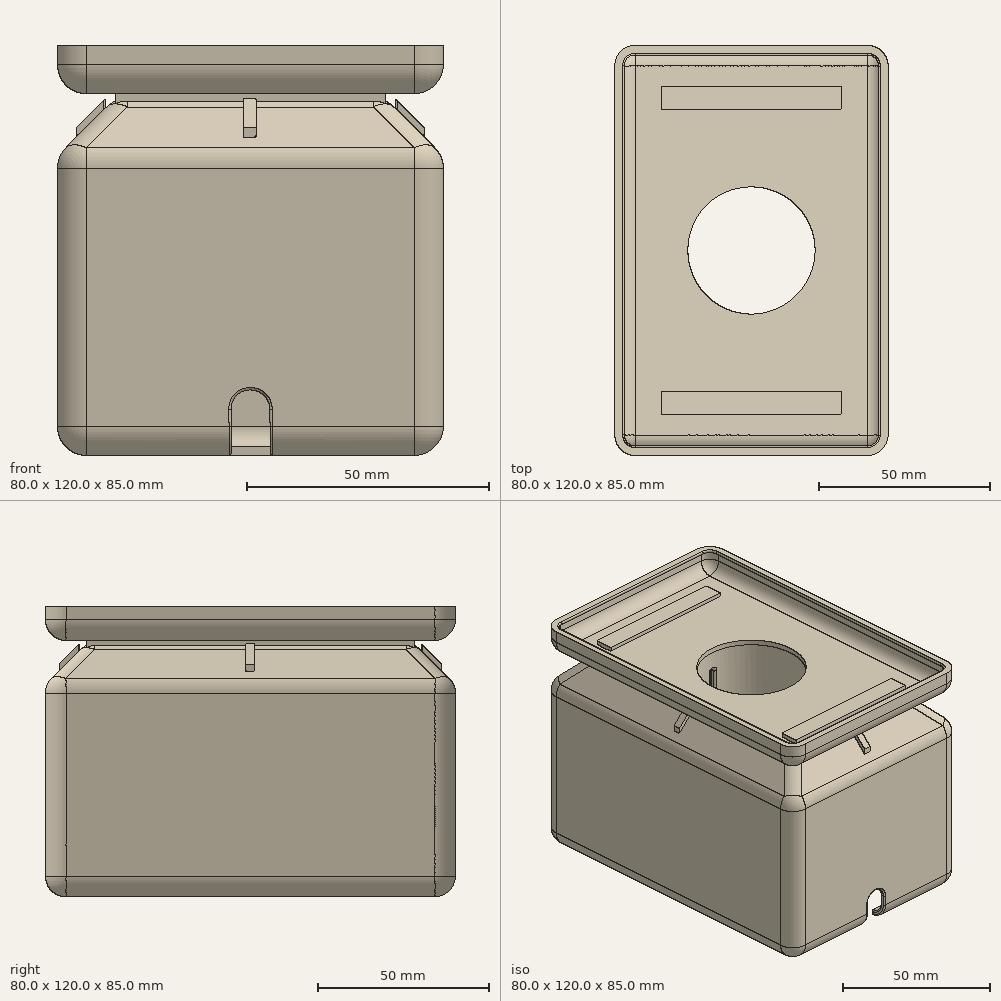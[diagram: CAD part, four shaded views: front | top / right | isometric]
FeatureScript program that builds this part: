
annotation { "Feature Type Name" : "Feature", "Feature Type Description" : "" }
export const myFeature = defineFeature(function(context is Context, id is Id, definition is map)
    precondition{}
    {
        {
            var Q0;
            Q0=qCreatedBy(makeId("Top.planeOp"),FACE);
            var sketch = newSketch(context, id + "F0", { "sketchPlane" : qUnion([Q0])});
            skLineSegment(sketch, "E0.bottom", {"start": v(0, 0) * mm, "end": v(80, 0) * mm});
            skLineSegment(sketch, "E0.top", {"start": v(0, 120) * mm, "end": v(80, 120) * mm});
            skLineSegment(sketch, "E0.left", {"start": v(0, 0) * mm, "end": v(0, 120) * mm});
            skLineSegment(sketch, "E0.right", {"start": v(80, 0) * mm, "end": v(80, 120) * mm});
            skSolve(sketch);
        }
        {
            var Q0;
            Q0=makeQuery(id+"F0.imprint","IMPRINT",FACE,{"disambiguationData":[TD([[makeQuery(id+"F0.imprint","IMPRINT",EDGE,{"derivedFrom":sQuery(id+"F0.wireOp",EDGE,"E0.bottom")}),1.0]])]});
            extrude(context, id + "F1", {"entities" : qUnion([Q0]), "oppositeDirection" : true, "depth" : 12 * mm});
        }
        {
            var Q0;
            Q0=makeQuery(id+"F1.opExtrude","CAP_FACE",FACE,{"disambiguationData":[OSD([sQuery(id+"F0.wireOp",EDGE,"E0.bottom"),sQuery(id+"F0.wireOp",EDGE,"E0.top"),sQuery(id+"F0.wireOp",EDGE,"E0.left"),sQuery(id+"F0.wireOp",EDGE,"E0.right")])],"isStart":true});
            chamfer(context, id + "F2", {"entities" : qUnion([Q0]), "width" : 12 * mm, "tangentPropagation" : true});
        }
        {
            var Q0;
            Q0=makeQuery(id+"F1.opExtrude","CAP_FACE",FACE,{"disambiguationData":[OSD([sQuery(id+"F0.wireOp",EDGE,"E0.bottom"),sQuery(id+"F0.wireOp",EDGE,"E0.top"),sQuery(id+"F0.wireOp",EDGE,"E0.left"),sQuery(id+"F0.wireOp",EDGE,"E0.right")])],"isStart":false});
            extrude(context, id + "F3", {"entities" : qUnion([Q0]), "operationType" : NewBodyOperationType.ADD, "depth" : 62 * mm});
        }
        {
            var Q0;
            Q0=makeQuery(id+"F3.opExtrude","CAP_FACE",FACE,{"disambiguationData":[OSD([sQuery(id+"F0.wireOp",EDGE,"E0.bottom"),sQuery(id+"F0.wireOp",EDGE,"E0.top"),sQuery(id+"F0.wireOp",EDGE,"E0.left"),sQuery(id+"F0.wireOp",EDGE,"E0.right")])],"isStart":false});
            var Q1;
            {var subQ0=sQuery(id+"F0.wireOp",EDGE,"E0.right");var subQ1=sQuery(id+"F0.wireOp",EDGE,"E0.left");var subQ2=sQuery(id+"F0.wireOp",EDGE,"E0.top");var subQ3=sQuery(id+"F0.wireOp",EDGE,"E0.bottom");Q1=makeQuery(id+"F3.opExtrude","SWEPT_FACE",FACE,{"disambiguationData":[OSD([subQ3,subQ2,subQ1,subQ0]),TDD([makeQuery(id+"F2.opChamfer","BLEND_EDGE",EDGE,{"blendedFrom":[makeQuery(id+"F1.opExtrude","CAP_EDGE",EDGE,{"disambiguationData":[OSD([subQ3])],"isStart":true}),makeQuery(id+"F1.opExtrude","CAP_FACE",FACE,{"disambiguationData":[OSD([subQ3,subQ2,subQ1,subQ0])],"isStart":false})],"blendedInto":[makeQuery(id+"F1.opExtrude","CAP_FACE",FACE,{"disambiguationData":[OSD([subQ3,subQ2,subQ1,subQ0])],"isStart":false})]})])]});}
            var Q2;
            {var subQ0=sQuery(id+"F0.wireOp",EDGE,"E0.right");var subQ1=sQuery(id+"F0.wireOp",EDGE,"E0.left");var subQ2=sQuery(id+"F0.wireOp",EDGE,"E0.top");var subQ3=sQuery(id+"F0.wireOp",EDGE,"E0.bottom");Q2=makeQuery(id+"F3.opExtrude","SWEPT_FACE",FACE,{"disambiguationData":[OSD([subQ3,subQ2,subQ1,subQ0]),TDD([makeQuery(id+"F2.opChamfer","BLEND_EDGE",EDGE,{"blendedFrom":[makeQuery(id+"F1.opExtrude","CAP_EDGE",EDGE,{"disambiguationData":[OSD([subQ2])],"isStart":true}),makeQuery(id+"F1.opExtrude","CAP_FACE",FACE,{"disambiguationData":[OSD([subQ3,subQ2,subQ1,subQ0])],"isStart":false})],"blendedInto":[makeQuery(id+"F1.opExtrude","CAP_FACE",FACE,{"disambiguationData":[OSD([subQ3,subQ2,subQ1,subQ0])],"isStart":false})]})])]});}
            var Q3;
            Q3=makeQuery(id+"F2.opChamfer","BLEND_FACE",FACE,{"disambiguationData":[OSD([sQuery(id+"F0.wireOp",EDGE,"E0.right")])]});
            var Q4;
            Q4=makeQuery(id+"F2.opChamfer","BLEND_FACE",FACE,{"disambiguationData":[OSD([sQuery(id+"F0.wireOp",EDGE,"E0.left")])]});
            var Q5;
            Q5=makeQuery(id+"F1.opExtrude","CAP_FACE",FACE,{"disambiguationData":[OSD([sQuery(id+"F0.wireOp",EDGE,"E0.bottom"),sQuery(id+"F0.wireOp",EDGE,"E0.top"),sQuery(id+"F0.wireOp",EDGE,"E0.left"),sQuery(id+"F0.wireOp",EDGE,"E0.right")])],"isStart":true});
            fillet(context, id + "F4", {"entities" : qUnion([Q0, Q1, Q2, Q3, Q4, Q5]), "radius" : 6 * mm, "tangentPropagation" : true, "allowEdgeOverflow" : false});
        }
        {
            var Q0;
            Q0=makeQuery(id+"F3.opExtrude","CAP_FACE",FACE,{"disambiguationData":[OSD([sQuery(id+"F0.wireOp",EDGE,"E0.bottom"),sQuery(id+"F0.wireOp",EDGE,"E0.top"),sQuery(id+"F0.wireOp",EDGE,"E0.left"),sQuery(id+"F0.wireOp",EDGE,"E0.right")])],"isStart":false});
            shell(context, id + "F5", {"entities" : qUnion([Q0]), "thickness" : 1.8 * mm});
        }
        {
            var Q0;
            Q0=qCreatedBy(makeId("Top.planeOp"),FACE);
            cPlane(context, id + "F6", {"entities" : qUnion([Q0]), "cplaneType" : CPlaneType.OFFSET, "offset" : 1 * mm, "width" : 150 * mm, "height" : 150 * mm});
        }
        {
            var Q0;
            Q0=qCreatedBy(id+"F6.planeOp",FACE);
            var sketch = newSketch(context, id + "F7", { "sketchPlane" : qUnion([Q0])});
            skLineSegment(sketch, "E1.bottom", {"start": v(12, 12) * mm, "end": v(68, 12) * mm});
            skLineSegment(sketch, "E1.top", {"start": v(12, 108) * mm, "end": v(68, 108) * mm});
            skLineSegment(sketch, "E1.left", {"start": v(12, 12) * mm, "end": v(12, 108) * mm});
            skLineSegment(sketch, "E1.right", {"start": v(68, 12) * mm, "end": v(68, 108) * mm});
            skLineSegment(sketch, "E2.0", {"start": v(14.49, 105.51) * mm, "end": v(14.49, 14.49) * mm, "construction": true});
            skLineSegment(sketch, "E3.0", {"start": v(65.51, 105.51) * mm, "end": v(14.49, 105.51) * mm, "construction": true});
            skLineSegment(sketch, "E4.0", {"start": v(65.51, 14.49) * mm, "end": v(65.51, 105.51) * mm, "construction": true});
            skLineSegment(sketch, "E5.0", {"start": v(14.49, 14.49) * mm, "end": v(65.51, 14.49) * mm, "construction": true});
            skLineSegment(sketch, "E6", {"start": v(14.49, 60) * mm, "end": v(65.51, 60) * mm, "construction": true});
            skLineSegment(sketch, "E7", {"start": v(40, 105.51) * mm, "end": v(40, 14.49) * mm, "construction": true});
            skCircle(sketch, "E8", {"center": v(40, 60) * mm, "radius": 14.5 * mm, "construction": true});
            skLineSegment(sketch, "E9.bottom", {"start": v(13.65, 16.24) * mm, "end": v(66.35, 16.24) * mm, "construction": true});
            skLineSegment(sketch, "E9.top", {"start": v(13.65, 19.49) * mm, "end": v(66.35, 19.49) * mm, "construction": true});
            skLineSegment(sketch, "E9.left", {"start": v(13.65, 16.24) * mm, "end": v(13.65, 19.49) * mm, "construction": true});
            skLineSegment(sketch, "E9.right", {"start": v(66.35, 16.24) * mm, "end": v(66.35, 19.49) * mm, "construction": true});
            skLineSegment(sketch, "E10.MirrorCS", {"start": v(13.65, 100.51) * mm, "end": v(66.35, 100.51) * mm, "construction": true});
            skLineSegment(sketch, "E11.MirrorCS", {"start": v(66.35, 103.76) * mm, "end": v(66.35, 100.51) * mm, "construction": true});
            skLineSegment(sketch, "E12.MirrorCS", {"start": v(13.65, 103.76) * mm, "end": v(66.35, 103.76) * mm, "construction": true});
            skLineSegment(sketch, "E13.MirrorCS", {"start": v(13.65, 103.76) * mm, "end": v(13.65, 100.51) * mm, "construction": true});
            skSolve(sketch);
        }
        {
            var Q0;
            Q0=makeQuery(id+"F7.imprint","IMPRINT",FACE,{"disambiguationData":[TD([[makeQuery(id+"F7.imprint","IMPRINT",EDGE,{"derivedFrom":sQuery(id+"F7.wireOp",EDGE,"E1.bottom")}),1.0]])]});
            extrude(context, id + "F8", {"entities" : qUnion([Q0]), "operationType" : NewBodyOperationType.ADD, "endBound" : BoundingType.UP_TO_NEXT, "oppositeDirection" : true, "depth" : 25 * mm});
        }
        {
            var Q0;
            Q0=makeQuery(id+"F8.opExtrude","CAP_FACE",FACE,{"disambiguationData":[OSD([sQuery(id+"F7.wireOp",EDGE,"E1.bottom"),sQuery(id+"F7.wireOp",EDGE,"E1.top"),sQuery(id+"F7.wireOp",EDGE,"E1.left"),sQuery(id+"F7.wireOp",EDGE,"E1.right")])],"isStart":true});
            var sketch = newSketch(context, id + "F9", { "sketchPlane" : qUnion([Q0])});
            skLineSegment(sketch, "E14.bottom", {"start": v(13.65, 13.75) * mm, "end": v(66.35, 13.75) * mm});
            skLineSegment(sketch, "E14.top", {"start": v(13.65, 17) * mm, "end": v(66.35, 17) * mm});
            skLineSegment(sketch, "E14.left", {"start": v(13.65, 13.75) * mm, "end": v(13.65, 17) * mm});
            skLineSegment(sketch, "E14.right", {"start": v(66.35, 13.75) * mm, "end": v(66.35, 17) * mm});
            skLineSegment(sketch, "E15", {"start": v(12, 60) * mm, "end": v(68, 60) * mm, "construction": true});
            skLineSegment(sketch, "E16.MirrorCS", {"start": v(13.65, 103) * mm, "end": v(66.35, 103) * mm});
            skLineSegment(sketch, "E17.MirrorCS", {"start": v(13.65, 106.25) * mm, "end": v(13.65, 103) * mm});
            skLineSegment(sketch, "E18.MirrorCS", {"start": v(13.65, 106.25) * mm, "end": v(66.35, 106.25) * mm});
            skLineSegment(sketch, "E19.MirrorCS", {"start": v(66.35, 106.25) * mm, "end": v(66.35, 103) * mm});
            skCircle(sketch, "E20", {"center": v(40, 60) * mm, "radius": 18.62 * mm});
            skSolve(sketch);
        }
        {
            var Q0;
            Q0=makeQuery(id+"F9.imprint","IMPRINT",FACE,{"disambiguationData":[TD([[makeQuery(id+"F9.imprint","IMPRINT",EDGE,{"derivedFrom":sQuery(id+"F9.wireOp",EDGE,"E20")}),1.0]])]});
            var Q1;
            Q1=makeQuery(id+"F9.imprint","IMPRINT",FACE,{"disambiguationData":[TD([[makeQuery(id+"F9.imprint","IMPRINT",EDGE,{"derivedFrom":sQuery(id+"F9.wireOp",EDGE,"E16.MirrorCS")}),1.0]])]});
            var Q2;
            Q2=makeQuery(id+"F9.imprint","IMPRINT",FACE,{"disambiguationData":[TD([[makeQuery(id+"F9.imprint","IMPRINT",EDGE,{"derivedFrom":sQuery(id+"F9.wireOp",EDGE,"E14.bottom")}),1.0]])]});
            extrude(context, id + "F10", {"entities" : qUnion([Q0, Q1, Q2]), "operationType" : NewBodyOperationType.REMOVE, "endBound" : BoundingType.UP_TO_NEXT, "oppositeDirection" : true, "depth" : 25 * mm});
        }
        {
            var Q0;
            {var subQ0=sQuery(id+"F0.wireOp",EDGE,"E0.right");var subQ1=sQuery(id+"F0.wireOp",EDGE,"E0.left");var subQ2=sQuery(id+"F0.wireOp",EDGE,"E0.top");var subQ3=sQuery(id+"F0.wireOp",EDGE,"E0.bottom");Q0=makeQuery(id+"F3.opExtrude","SWEPT_FACE",FACE,{"disambiguationData":[OSD([subQ3,subQ2,subQ1,subQ0]),TDD([makeQuery(id+"F2.opChamfer","BLEND_EDGE",EDGE,{"blendedFrom":[makeQuery(id+"F1.opExtrude","CAP_EDGE",EDGE,{"disambiguationData":[OSD([subQ3])],"isStart":true}),makeQuery(id+"F1.opExtrude","CAP_FACE",FACE,{"disambiguationData":[OSD([subQ3,subQ2,subQ1,subQ0])],"isStart":false})],"blendedInto":[makeQuery(id+"F1.opExtrude","CAP_FACE",FACE,{"disambiguationData":[OSD([subQ3,subQ2,subQ1,subQ0])],"isStart":false})]})])]});}
            var sketch = newSketch(context, id + "F11", { "sketchPlane" : qUnion([Q0])});
            skLineSegment(sketch, "E21", {"start": v(40, -94.47) * mm, "end": v(40, -64.4) * mm, "construction": true});
            skPoint(sketch, "E21.startSnap0", {"position": v(40, -68) * mm});
            skArc(sketch, "E22", {"start": v(44, -64.4) * mm, "mid": v(39.97, -60.41) * mm, "end": v(36, -64.47) * mm});
            skLineSegment(sketch, "E23", {"start": v(36, -64.47) * mm, "end": v(36.15, -74.05) * mm});
            skLineSegment(sketch, "E24", {"start": v(44, -64.4) * mm, "end": v(44.15, -74.05) * mm});
            skLineSegment(sketch, "E25", {"start": v(44.15, -74.05) * mm, "end": v(36.15, -74.05) * mm});
            skSolve(sketch);
        }
        {
            var Q0;
            Q0 = qSketchRegion(id + "F11", true);
            extrude(context, id + "F12", {"entities" : qUnion([Q0]), "operationType" : NewBodyOperationType.REMOVE, "endBound" : BoundingType.UP_TO_NEXT, "oppositeDirection" : true, "depth" : 25 * mm});
        }
        {
            var Q0;
            Q0=makeQuery(id+"F12.boolean.opBoolean","COPY",FACE,{"derivedFrom":makeQuery(id+"F12.opExtrude","SWEPT_FACE",FACE,{"disambiguationData":[OSD([sQuery(id+"F11.wireOp",EDGE,"E22")])]})});
            var Q1;
            Q1=makeQuery(id+"F12.boolean.opBoolean","COPY",FACE,{"derivedFrom":makeQuery(id+"F12.opExtrude","SWEPT_FACE",FACE,{"disambiguationData":[OSD([sQuery(id+"F11.wireOp",EDGE,"E23")])]})});
            var Q2;
            Q2=makeQuery(id+"F12.boolean.opBoolean","COPY",FACE,{"derivedFrom":makeQuery(id+"F12.opExtrude","SWEPT_FACE",FACE,{"disambiguationData":[OSD([sQuery(id+"F11.wireOp",EDGE,"E24")])]})});
            var Q3;
            {var subQ0=sQuery(id+"F0.wireOp",EDGE,"E0.right");var subQ1=sQuery(id+"F0.wireOp",EDGE,"E0.left");var subQ2=sQuery(id+"F0.wireOp",EDGE,"E0.top");var subQ3=sQuery(id+"F0.wireOp",EDGE,"E0.bottom");Q3=makeQuery(id+"F5.opShell","SHELL_CAP_FACE",FACE,{"derivedFrom":[makeQuery(id+"F4.opFillet","BLEND_EDGE",EDGE,{"blendedFrom":[makeQuery(id+"F3.opExtrude","CAP_EDGE",EDGE,{"disambiguationData":[OSD([subQ3,subQ2,subQ1,subQ0]),TDD([makeQuery(id+"F2.opChamfer","BLEND_EDGE",EDGE,{"blendedFrom":[makeQuery(id+"F1.opExtrude","CAP_EDGE",EDGE,{"disambiguationData":[OSD([subQ0])],"isStart":true}),makeQuery(id+"F1.opExtrude","CAP_FACE",FACE,{"disambiguationData":[OSD([subQ3,subQ2,subQ1,subQ0])],"isStart":false})],"blendedInto":[makeQuery(id+"F1.opExtrude","CAP_FACE",FACE,{"disambiguationData":[OSD([subQ3,subQ2,subQ1,subQ0])],"isStart":false})]})])],"isStart":false}),makeQuery(id+"F3.opExtrude","CAP_FACE",FACE,{"disambiguationData":[OSD([subQ3,subQ2,subQ1,subQ0])],"isStart":false})],"blendedInto":[makeQuery(id+"F3.opExtrude","CAP_FACE",FACE,{"disambiguationData":[OSD([subQ3,subQ2,subQ1,subQ0])],"isStart":false})]})]});}
            var Q4;
            {var subQ0=sQuery(id+"F0.wireOp",EDGE,"E0.right");var subQ1=sQuery(id+"F0.wireOp",EDGE,"E0.left");var subQ2=sQuery(id+"F0.wireOp",EDGE,"E0.top");var subQ3=sQuery(id+"F0.wireOp",EDGE,"E0.bottom");Q4=makeQuery(id+"F5.opShell","SHELL_CAP_FACE",FACE,{"derivedFrom":[makeQuery(id+"F4.opFillet","BLEND_EDGE",EDGE,{"blendedFrom":[makeQuery(id+"F3.opExtrude","CAP_EDGE",EDGE,{"disambiguationData":[OSD([subQ3,subQ2,subQ1,subQ0]),TDD([makeQuery(id+"F2.opChamfer","BLEND_EDGE",EDGE,{"blendedFrom":[makeQuery(id+"F1.opExtrude","CAP_EDGE",EDGE,{"disambiguationData":[OSD([subQ2])],"isStart":true}),makeQuery(id+"F1.opExtrude","CAP_FACE",FACE,{"disambiguationData":[OSD([subQ3,subQ2,subQ1,subQ0])],"isStart":false})],"blendedInto":[makeQuery(id+"F1.opExtrude","CAP_FACE",FACE,{"disambiguationData":[OSD([subQ3,subQ2,subQ1,subQ0])],"isStart":false})]})])],"isStart":false}),makeQuery(id+"F3.opExtrude","CAP_FACE",FACE,{"disambiguationData":[OSD([subQ3,subQ2,subQ1,subQ0])],"isStart":false})],"blendedInto":[makeQuery(id+"F3.opExtrude","CAP_FACE",FACE,{"disambiguationData":[OSD([subQ3,subQ2,subQ1,subQ0])],"isStart":false})]})]});}
            var Q5;
            {var subQ0=sQuery(id+"F0.wireOp",EDGE,"E0.right");var subQ1=sQuery(id+"F0.wireOp",EDGE,"E0.left");var subQ2=sQuery(id+"F0.wireOp",EDGE,"E0.top");var subQ3=sQuery(id+"F0.wireOp",EDGE,"E0.bottom");Q5=makeQuery(id+"F5.opShell","SHELL_CAP_FACE",FACE,{"derivedFrom":[makeQuery(id+"F4.opFillet","BLEND_EDGE",EDGE,{"blendedFrom":[makeQuery(id+"F3.opExtrude","CAP_EDGE",EDGE,{"disambiguationData":[OSD([subQ3,subQ2,subQ1,subQ0]),TDD([makeQuery(id+"F2.opChamfer","BLEND_EDGE",EDGE,{"blendedFrom":[makeQuery(id+"F1.opExtrude","CAP_EDGE",EDGE,{"disambiguationData":[OSD([subQ1])],"isStart":true}),makeQuery(id+"F1.opExtrude","CAP_FACE",FACE,{"disambiguationData":[OSD([subQ3,subQ2,subQ1,subQ0])],"isStart":false})],"blendedInto":[makeQuery(id+"F1.opExtrude","CAP_FACE",FACE,{"disambiguationData":[OSD([subQ3,subQ2,subQ1,subQ0])],"isStart":false})]})])],"isStart":false}),makeQuery(id+"F3.opExtrude","CAP_FACE",FACE,{"disambiguationData":[OSD([subQ3,subQ2,subQ1,subQ0])],"isStart":false})],"blendedInto":[makeQuery(id+"F3.opExtrude","CAP_FACE",FACE,{"disambiguationData":[OSD([subQ3,subQ2,subQ1,subQ0])],"isStart":false})]})]});}
            var Q6;
            {var subQ0=sQuery(id+"F0.wireOp",EDGE,"E0.right");var subQ1=sQuery(id+"F0.wireOp",EDGE,"E0.left");var subQ2=sQuery(id+"F0.wireOp",EDGE,"E0.top");var subQ3=sQuery(id+"F0.wireOp",EDGE,"E0.bottom");var subQ4=makeQuery(id+"F1.opExtrude","CAP_FACE",FACE,{"disambiguationData":[OSD([subQ3,subQ2,subQ1,subQ0])],"isStart":false});var subQ8=makeQuery(id+"F1.opExtrude","CAP_EDGE",EDGE,{"disambiguationData":[OSD([subQ3])],"isStart":true});var subQ9=makeQuery(id+"F3.opExtrude","CAP_EDGE",EDGE,{"disambiguationData":[OSD([subQ3,subQ2,subQ1,subQ0]),TDD([makeQuery(id+"F2.opChamfer","BLEND_EDGE",EDGE,{"blendedFrom":[subQ8,subQ4],"blendedInto":[subQ4]})])],"isStart":false});var subQ11=makeQuery(id+"F3.opExtrude","CAP_FACE",FACE,{"disambiguationData":[OSD([subQ3,subQ2,subQ1,subQ0])],"isStart":false});Q6=makeQuery(id+"F12.boolean.opBoolean","SPLIT",FACE,{"disambiguationData":[TD([makeQuery(id+"F12.opExtrude","SWEPT_FACE",FACE,{"disambiguationData":[OSD([sQuery(id+"F11.wireOp",EDGE,"E23")])]})])],"derivedFrom":makeQuery(id+"F5.opShell","SHELL_CAP_FACE",FACE,{"derivedFrom":[makeQuery(id+"F4.opFillet","BLEND_EDGE",EDGE,{"blendedFrom":[subQ9,subQ11],"blendedInto":[subQ11]})]})});}
            var Q7;
            {var subQ0=sQuery(id+"F0.wireOp",EDGE,"E0.right");var subQ1=sQuery(id+"F0.wireOp",EDGE,"E0.left");var subQ2=sQuery(id+"F0.wireOp",EDGE,"E0.top");var subQ3=sQuery(id+"F0.wireOp",EDGE,"E0.bottom");var subQ4=makeQuery(id+"F3.opExtrude","CAP_FACE",FACE,{"disambiguationData":[OSD([subQ3,subQ2,subQ1,subQ0])],"isStart":false});var subQ5=makeQuery(id+"F1.opExtrude","CAP_FACE",FACE,{"disambiguationData":[OSD([subQ3,subQ2,subQ1,subQ0])],"isStart":false});var subQ8=makeQuery(id+"F1.opExtrude","CAP_EDGE",EDGE,{"disambiguationData":[OSD([subQ3])],"isStart":true});var subQ11=makeQuery(id+"F3.opExtrude","CAP_EDGE",EDGE,{"disambiguationData":[OSD([subQ3,subQ2,subQ1,subQ0]),TDD([makeQuery(id+"F2.opChamfer","BLEND_EDGE",EDGE,{"blendedFrom":[subQ8,subQ5],"blendedInto":[subQ5]})])],"isStart":false});Q7=makeQuery(id+"F12.boolean.opBoolean","SPLIT",FACE,{"disambiguationData":[TD([makeQuery(id+"F12.opExtrude","SWEPT_FACE",FACE,{"disambiguationData":[OSD([sQuery(id+"F11.wireOp",EDGE,"E24")])]})])],"derivedFrom":makeQuery(id+"F5.opShell","SHELL_CAP_FACE",FACE,{"derivedFrom":[makeQuery(id+"F4.opFillet","BLEND_EDGE",EDGE,{"blendedFrom":[subQ11,subQ4],"blendedInto":[subQ4]})]})});}
            fillet(context, id + "F13", {"entities" : qUnion([Q0, Q1, Q2, Q3, Q4, Q5, Q6, Q7]), "radius" : .5 * mm, "tangentPropagation" : true, "allowEdgeOverflow" : false});
        }
        {
            var Q0;
            Q0=qCreatedBy(id+"F6.planeOp",FACE);
            var sketch = newSketch(context, id + "F14", { "sketchPlane" : qUnion([Q0])});
            skLineSegment(sketch, "E26.0", {"start": v(11.75, 11.75) * mm, "end": v(11.75, 108.25) * mm});
            skLineSegment(sketch, "E26.1", {"start": v(11.75, 11.75) * mm, "end": v(68.25, 11.75) * mm});
            skLineSegment(sketch, "E26.2", {"start": v(68.25, 11.75) * mm, "end": v(68.25, 108.25) * mm});
            skLineSegment(sketch, "E26.3", {"start": v(11.75, 108.25) * mm, "end": v(68.25, 108.25) * mm});
            skLineSegment(sketch, "E27.0", {"start": v(80, 114) * mm, "end": v(80, 6) * mm});
            skLineSegment(sketch, "E28.0", {"start": v(6, 120) * mm, "end": v(74, 120) * mm});
            skLineSegment(sketch, "E29.0", {"start": v(74, 0) * mm, "end": v(6, 0) * mm});
            skLineSegment(sketch, "E30.0", {"start": v(0, 6) * mm, "end": v(0, 114) * mm});
            skLineSegment(sketch, "E31.bottom", {"start": v(0, 0) * mm, "end": v(80, 0) * mm});
            skLineSegment(sketch, "E31.top", {"start": v(0, 120) * mm, "end": v(80, 120) * mm});
            skLineSegment(sketch, "E31.left", {"start": v(0, 0) * mm, "end": v(0, 120) * mm});
            skLineSegment(sketch, "E31.right", {"start": v(80, 0) * mm, "end": v(80, 120) * mm});
            skSolve(sketch);
        }
        {
            var Q0;
            Q0=makeQuery(id+"F14.imprint","IMPRINT",FACE,{"disambiguationData":[TD([[makeQuery(id+"F14.imprint","IMPRINT",EDGE,{"derivedFrom":sQuery(id+"F14.wireOp",EDGE,"E26.0")}),1.0]])]});
            extrude(context, id + "F15", {"entities" : qUnion([Q0]), "oppositeDirection" : true, "depth" : 13 * mm});
        }
        {
            var Q0;
            Q0=makeQuery(id+"F15.opExtrude","SWEPT_EDGE",EDGE,{"disambiguationData":[OSD([sQuery(id+"F14.wireOp",EDGE,"E31.bottom"),sQuery(id+"F14.wireOp",EDGE,"E31.right")])]});
            var Q1;
            Q1=makeQuery(id+"F15.opExtrude","SWEPT_EDGE",EDGE,{"disambiguationData":[OSD([sQuery(id+"F14.wireOp",EDGE,"E31.top"),sQuery(id+"F14.wireOp",EDGE,"E31.right")])]});
            var Q2;
            Q2=makeQuery(id+"F15.opExtrude","SWEPT_EDGE",EDGE,{"disambiguationData":[OSD([sQuery(id+"F14.wireOp",EDGE,"E31.bottom"),sQuery(id+"F14.wireOp",EDGE,"E31.left")])]});
            var Q3;
            Q3=makeQuery(id+"F15.opExtrude","SWEPT_EDGE",EDGE,{"disambiguationData":[OSD([sQuery(id+"F14.wireOp",EDGE,"E31.top"),sQuery(id+"F14.wireOp",EDGE,"E31.left")])]});
            var Q4;
            Q4=makeQuery(id+"F15.opExtrude","CAP_EDGE",EDGE,{"disambiguationData":[OSD([sQuery(id+"F14.wireOp",EDGE,"E31.top")])],"isStart":true});
            var Q5;
            Q5=makeQuery(id+"F15.opExtrude","CAP_EDGE",EDGE,{"disambiguationData":[OSD([sQuery(id+"F14.wireOp",EDGE,"E31.left")])],"isStart":true});
            var Q6;
            Q6=makeQuery(id+"F15.opExtrude","CAP_EDGE",EDGE,{"disambiguationData":[OSD([sQuery(id+"F14.wireOp",EDGE,"E31.right")])],"isStart":true});
            var Q7;
            Q7=makeQuery(id+"F15.opExtrude","CAP_EDGE",EDGE,{"disambiguationData":[OSD([sQuery(id+"F14.wireOp",EDGE,"E31.bottom")])],"isStart":true});
            fillet(context, id + "F16", {"entities" : qUnion([Q0, Q1, Q2, Q3, Q4, Q5, Q6, Q7]), "radius" : 6 * mm, "tangentPropagation" : true, "allowEdgeOverflow" : false});
        }
        {
            var Q0;
            Q0=makeQuery(id+"F1.opExtrude","SWEPT_BODY",BODY,{"disambiguationData":[OSD([sQuery(id+"F0.wireOp",EDGE,"E0.bottom"),sQuery(id+"F0.wireOp",EDGE,"E0.top"),sQuery(id+"F0.wireOp",EDGE,"E0.left"),sQuery(id+"F0.wireOp",EDGE,"E0.right")])]});
            var Q1;
            Q1=makeQuery(id+"F15.opExtrude","SWEPT_BODY",BODY,{"disambiguationData":[OSD([sQuery(id+"F14.wireOp",EDGE,"E26.0"),sQuery(id+"F14.wireOp",EDGE,"E26.1"),sQuery(id+"F14.wireOp",EDGE,"E26.2"),sQuery(id+"F14.wireOp",EDGE,"E26.3"),sQuery(id+"F14.wireOp",EDGE,"E31.bottom"),sQuery(id+"F14.wireOp",EDGE,"E31.top"),sQuery(id+"F14.wireOp",EDGE,"E31.left"),sQuery(id+"F14.wireOp",EDGE,"E31.right")])]});
            booleanBodies(context, id + "F17", {"operationType" : BooleanOperationType.SUBTRACTION, "tools" : qUnion([Q0]), "targets" : qUnion([Q1]), "keepTools" : true});
        }
        {
            var Q0;
            Q0=qCreatedBy(makeId("Top.planeOp"),FACE);
            var sketch = newSketch(context, id + "F18", { "sketchPlane" : qUnion([Q0])});
            skLineSegment(sketch, "E32.0", {"start": v(12, 108) * mm, "end": v(68, 108) * mm, "construction": true});
            skLineSegment(sketch, "E33.0", {"start": v(68, 12) * mm, "end": v(68, 108) * mm, "construction": true});
            skLineSegment(sketch, "E34.0", {"start": v(12, 12) * mm, "end": v(68, 12) * mm, "construction": true});
            skLineSegment(sketch, "E35.0", {"start": v(12, 12) * mm, "end": v(12, 108) * mm, "construction": true});
            skLineSegment(sketch, "E36.0.0", {"start": v(78.24, 114) * mm, "end": v(69.76, 105.51) * mm, "construction": true});
            skLineSegment(sketch, "E36.0.1", {"start": v(69.76, 105.51) * mm, "end": v(69.76, 14.49) * mm, "construction": true});
            skLineSegment(sketch, "E36.0.2", {"start": v(69.76, 14.49) * mm, "end": v(78.24, 6) * mm, "construction": true});
            skLineSegment(sketch, "E36.0.3", {"start": v(78.24, 6) * mm, "end": v(78.24, 114) * mm, "construction": true});
            skLineSegment(sketch, "E37.0.0", {"start": v(6, 118.24) * mm, "end": v(14.49, 109.76) * mm, "construction": true});
            skLineSegment(sketch, "E37.0.1", {"start": v(14.49, 109.76) * mm, "end": v(65.51, 109.76) * mm, "construction": true});
            skLineSegment(sketch, "E37.0.2", {"start": v(65.51, 109.76) * mm, "end": v(74, 118.24) * mm, "construction": true});
            skLineSegment(sketch, "E37.0.3", {"start": v(74, 118.24) * mm, "end": v(6, 118.24) * mm, "construction": true});
            skLineSegment(sketch, "E38.0.0", {"start": v(1.76, 6) * mm, "end": v(10.24, 14.49) * mm, "construction": true});
            skLineSegment(sketch, "E38.0.1", {"start": v(10.24, 14.49) * mm, "end": v(10.24, 105.51) * mm, "construction": true});
            skLineSegment(sketch, "E38.0.2", {"start": v(10.24, 105.51) * mm, "end": v(1.76, 114) * mm, "construction": true});
            skLineSegment(sketch, "E38.0.3", {"start": v(1.76, 114) * mm, "end": v(1.76, 6) * mm, "construction": true});
            skLineSegment(sketch, "E39.0.0", {"start": v(74, 1.76) * mm, "end": v(65.51, 10.24) * mm, "construction": true});
            skLineSegment(sketch, "E39.0.1", {"start": v(65.51, 10.24) * mm, "end": v(14.49, 10.24) * mm, "construction": true});
            skLineSegment(sketch, "E39.0.2", {"start": v(14.49, 10.24) * mm, "end": v(6, 1.76) * mm, "construction": true});
            skLineSegment(sketch, "E39.0.3", {"start": v(6, 1.76) * mm, "end": v(74, 1.76) * mm, "construction": true});
            skLineSegment(sketch, "E40.bottom", {"start": v(69.98, 61.25) * mm, "end": v(75.98, 61.25) * mm});
            skLineSegment(sketch, "E40.top", {"start": v(69.98, 58.65) * mm, "end": v(75.98, 58.65) * mm});
            skLineSegment(sketch, "E40.left", {"start": v(69.98, 61.25) * mm, "end": v(69.98, 58.65) * mm});
            skLineSegment(sketch, "E40.right", {"start": v(75.98, 61.25) * mm, "end": v(75.98, 58.65) * mm});
            skLineSegment(sketch, "E41", {"start": v(40, 108) * mm, "end": v(40, 12) * mm, "construction": true});
            skLineSegment(sketch, "E42", {"start": v(12, 60) * mm, "end": v(69.98, 59.95) * mm, "construction": true});
            skLineSegment(sketch, "E43.MirrorCS", {"start": v(10.02, 61.25) * mm, "end": v(4.02, 61.25) * mm});
            skLineSegment(sketch, "E44.MirrorCS", {"start": v(10.02, 58.65) * mm, "end": v(4.02, 58.65) * mm});
            skLineSegment(sketch, "E45.MirrorCS", {"start": v(4.02, 61.25) * mm, "end": v(4.02, 58.65) * mm});
            skLineSegment(sketch, "E46.MirrorCS", {"start": v(10.02, 61.25) * mm, "end": v(10.02, 58.65) * mm});
            skLineSegment(sketch, "E47.bottom", {"start": v(38.7, 4.02) * mm, "end": v(41.3, 4.02) * mm});
            skLineSegment(sketch, "E47.top", {"start": v(38.7, 10.02) * mm, "end": v(41.3, 10.02) * mm});
            skLineSegment(sketch, "E47.left", {"start": v(38.7, 4.02) * mm, "end": v(38.7, 10.02) * mm});
            skLineSegment(sketch, "E47.right", {"start": v(41.3, 4.02) * mm, "end": v(41.3, 10.02) * mm});
            skLineSegment(sketch, "E48.MirrorCS", {"start": v(41.4, 115.93) * mm, "end": v(41.39, 109.93) * mm});
            skLineSegment(sketch, "E49.MirrorCS", {"start": v(38.8, 115.93) * mm, "end": v(38.79, 109.93) * mm});
            skLineSegment(sketch, "E50.MirrorCS", {"start": v(38.8, 115.93) * mm, "end": v(41.4, 115.93) * mm});
            skLineSegment(sketch, "E51.MirrorCS", {"start": v(38.79, 109.93) * mm, "end": v(41.39, 109.93) * mm});
            skSolve(sketch);
        }
        {
            var Q0;
            Q0 = qSketchRegion(id + "F18", true);
            extrude(context, id + "F19", {"entities" : qUnion([Q0]), "operationType" : NewBodyOperationType.REMOVE, "oppositeDirection" : true, "depth" : 25 * mm});
        }
        {
            var Q0;
            Q0=makeQuery(id+"F19.boolean.opBoolean","COPY",FACE,{"derivedFrom":makeQuery(id+"F19.opExtrude","SWEPT_FACE",FACE,{"disambiguationData":[OSD([sQuery(id+"F18.wireOp",EDGE,"E48.MirrorCS")])]})});
            var sketch = newSketch(context, id + "F20", { "sketchPlane" : qUnion([Q0])});
            skLineSegment(sketch, "E52", {"start": v(-110, -1.93) * mm, "end": v(-110, 0.07) * mm});
            skPoint(sketch, "E52.endSnap0", {"position": v(-110, -3.2) * mm});
            skLineSegment(sketch, "E53", {"start": v(-116, -7.93) * mm, "end": v(-116, -5.93) * mm});
            skLineSegment(sketch, "E54", {"start": v(-116, -5.93) * mm, "end": v(-110, 0.07) * mm});
            skLineSegment(sketch, "E55", {"start": v(-110, -1.93) * mm, "end": v(-110, -7.01) * mm});
            skLineSegment(sketch, "E56", {"start": v(-116, -7.93) * mm, "end": v(-110, -7.93) * mm});
            skLineSegment(sketch, "E57", {"start": v(-110, -7.93) * mm, "end": v(-110, -7.01) * mm});
            skLineSegment(sketch, "E58.0.0", {"start": v(-4.1, -7.98) * mm, "end": v(-10.1, -1.98) * mm, "construction": true});
            skLineSegment(sketch, "E58.0.1", {"start": v(-10.1, -1.98) * mm, "end": v(-10.1, -4.53) * mm, "construction": true});
            skLineSegment(sketch, "E58.0.2", {"start": v(-4.1, -10.53) * mm, "end": v(-10.1, -4.53) * mm, "construction": true});
            skLineSegment(sketch, "E58.0.3", {"start": v(-4.1, -10.53) * mm, "end": v(-4.1, -7.98) * mm, "construction": true});
            skLineSegment(sketch, "E59", {"start": v(-4.1, -7.98) * mm, "end": v(-116, -7.93) * mm, "construction": true});
            skLineSegment(sketch, "E60", {"start": v(-60.05, -7.95) * mm, "end": v(-60.04, 9.1) * mm, "construction": true});
            skLineSegment(sketch, "E61.MirrorCS", {"start": v(-4.09, -5.98) * mm, "end": v(-10.08, 0.03) * mm});
            skLineSegment(sketch, "E62.MirrorCS", {"start": v(-4.1, -7.98) * mm, "end": v(-4.09, -5.98) * mm});
            skLineSegment(sketch, "E63.MirrorCS", {"start": v(-4.1, -7.98) * mm, "end": v(-10.1, -7.97) * mm});
            skLineSegment(sketch, "E64.MirrorCS", {"start": v(-10.1, -7.97) * mm, "end": v(-10.1, -7.06) * mm});
            skLineSegment(sketch, "E65.MirrorCS", {"start": v(-10.09, -1.97) * mm, "end": v(-10.1, -7.06) * mm});
            skLineSegment(sketch, "E66.MirrorCS", {"start": v(-10.09, -1.97) * mm, "end": v(-10.08, 0.03) * mm});
            skSolve(sketch);
        }
        {
            var Q0;
            Q0 = qSketchRegion(id + "F20", true);
            var Q1;
            Q1=makeQuery(id+"F19.boolean.opBoolean","COPY",FACE,{"derivedFrom":makeQuery(id+"F19.opExtrude","SWEPT_FACE",FACE,{"disambiguationData":[OSD([sQuery(id+"F18.wireOp",EDGE,"E49.MirrorCS")])]})});
            extrude(context, id + "F21", {"entities" : qUnion([Q0]), "endBound" : BoundingType.UP_TO_SURFACE, "endBoundEntityFace" : qUnion([Q1]), "depth" : 25 * mm});
        }
        {
            var Q0;
            Q0=makeQuery(id+"F19.boolean.opBoolean","COPY",FACE,{"derivedFrom":makeQuery(id+"F19.opExtrude","SWEPT_FACE",FACE,{"disambiguationData":[OSD([sQuery(id+"F18.wireOp",EDGE,"E44.MirrorCS")])]})});
            var sketch = newSketch(context, id + "F22", { "sketchPlane" : qUnion([Q0])});
            skLineSegment(sketch, "E67.0.0", {"start": v(-69.98, -1.98) * mm, "end": v(-75.98, -7.98) * mm, "construction": true});
            skLineSegment(sketch, "E67.0.1", {"start": v(-75.98, -7.98) * mm, "end": v(-75.98, -10.53) * mm, "construction": true});
            skLineSegment(sketch, "E67.0.2", {"start": v(-69.98, -4.53) * mm, "end": v(-75.98, -10.53) * mm, "construction": true});
            skLineSegment(sketch, "E67.0.3", {"start": v(-69.98, -4.53) * mm, "end": v(-69.98, -1.98) * mm, "construction": true});
            skLineSegment(sketch, "E68", {"start": v(-40, -7.98) * mm, "end": v(-40, 5.98) * mm, "construction": true});
            skLineSegment(sketch, "E69.MirrorCS", {"start": v(-69.98, -1.98) * mm, "end": v(-69.98, 0.02) * mm});
            skLineSegment(sketch, "E70.MirrorCS", {"start": v(-69.98, 0.02) * mm, "end": v(-75.98, -5.98) * mm});
            skLineSegment(sketch, "E71.MirrorCS", {"start": v(-75.98, -7.98) * mm, "end": v(-75.98, -5.98) * mm});
            skLineSegment(sketch, "E72.MirrorCS", {"start": v(-69.98, -7.98) * mm, "end": v(-69.98, -1.98) * mm});
            skLineSegment(sketch, "E73.MirrorCS", {"start": v(-75.98, -7.98) * mm, "end": v(-69.98, -7.98) * mm});
            skLineSegment(sketch, "E74.MirrorCS", {"start": v(-10.02, 0.02) * mm, "end": v(-4.02, -5.98) * mm});
            skLineSegment(sketch, "E75.MirrorCS", {"start": v(-10.02, -1.98) * mm, "end": v(-10.02, 0.02) * mm});
            skLineSegment(sketch, "E76.MirrorCS", {"start": v(-10.02, -7.98) * mm, "end": v(-10.02, -1.98) * mm});
            skLineSegment(sketch, "E77.MirrorCS", {"start": v(-4.02, -7.98) * mm, "end": v(-10.02, -7.98) * mm});
            skLineSegment(sketch, "E78.MirrorCS", {"start": v(-4.02, -7.98) * mm, "end": v(-4.02, -5.98) * mm});
            skSolve(sketch);
        }
        {
            var Q0;
            Q0 = qSketchRegion(id + "F22", true);
            var Q1;
            Q1=makeQuery(id+"F19.boolean.opBoolean","COPY",FACE,{"derivedFrom":makeQuery(id+"F19.opExtrude","SWEPT_FACE",FACE,{"disambiguationData":[OSD([sQuery(id+"F18.wireOp",EDGE,"E40.bottom")])]})});
            extrude(context, id + "F23", {"entities" : qUnion([Q0]), "endBound" : BoundingType.UP_TO_SURFACE, "endBoundEntityFace" : qUnion([Q1]), "depth" : 25 * mm});
        }
        {
            var Q0;
            Q0=makeQuery(id+"F21.opExtrude","CAP_EDGE",EDGE,{"disambiguationData":[OSD([sQuery(id+"F20.wireOp",EDGE,"E56")])],"isStart":true});
            var Q1;
            {var subQ0=sQuery(id+"F20.wireOp",EDGE,"E56");var subQ1=sQuery(id+"F18.wireOp",EDGE,"E48.MirrorCS");var subQ2=makeQuery(id+"F19.opExtrude","SWEPT_FACE",FACE,{"disambiguationData":[OSD([subQ1])]});var subQ3=sQuery(id+"F0.wireOp",EDGE,"E0.top");var subQ4=makeQuery(id+"F20.imprint","INTERSECT",VERTEX,{"derivedFrom":[makeQuery(id+"F19.boolean.opBoolean","INTERSECT",EDGE,{"derivedFrom":[makeQuery(id+"F5.opShell","OFFSET_FACE",FACE,{"disambiguationData":[OSD([subQ3])]}),subQ2]}),subQ0]});Q1=makeQuery(id+"F21.opExtrude","TWEAK_EDGE",EDGE,{"derivedFrom":[makeQuery(id+"F19.boolean.opBoolean","COPY",FACE,{"derivedFrom":makeQuery(id+"F19.opExtrude","SWEPT_FACE",FACE,{"disambiguationData":[OSD([sQuery(id+"F18.wireOp",EDGE,"E49.MirrorCS")])]})}),makeQuery(id+"F20.imprint","IMPRINT",EDGE,{"disambiguationData":[TD([[subQ4,1.0]])],"derivedFrom":subQ0}),makeQuery(id+"F20.imprint","IMPRINT",EDGE,{"disambiguationData":[TD([[makeQuery(id+"F20.imprint","INTERSECT",VERTEX,{"derivedFrom":[subQ0,sQuery(id+"F20.wireOp",EDGE,"E57")]}),1.0]])],"derivedFrom":subQ0})]});}
            var Q2;
            {var subQ0=sQuery(id+"F20.wireOp",EDGE,"E57");var subQ1=sQuery(id+"F20.wireOp",EDGE,"E55");var subQ2=sQuery(id+"F20.wireOp",EDGE,"E52");var subQ3=makeQuery(id+"F19.opExtrude","SWEPT_FACE",FACE,{"disambiguationData":[OSD([sQuery(id+"F18.wireOp",EDGE,"E48.MirrorCS")])]});var subQ4=sQuery(id+"F0.wireOp",EDGE,"E0.top");Q2=makeQuery(id+"F21.opExtrude","TWEAK_EDGE",EDGE,{"derivedFrom":[makeQuery(id+"F19.boolean.opBoolean","COPY",FACE,{"derivedFrom":makeQuery(id+"F19.opExtrude","SWEPT_FACE",FACE,{"disambiguationData":[OSD([sQuery(id+"F18.wireOp",EDGE,"E49.MirrorCS")])]})}),makeQuery(id+"F20.imprint","IMPRINT",EDGE,{"derivedFrom":subQ2}),makeQuery(id+"F20.imprint","IMPRINT",EDGE,{"disambiguationData":[TD([[makeQuery(id+"F20.imprint","INTERSECT",VERTEX,{"derivedFrom":[subQ1,subQ0]}),1.0]])],"derivedFrom":subQ1}),makeQuery(id+"F20.imprint","IMPRINT",EDGE,{"disambiguationData":[TD([[makeQuery(id+"F20.imprint","INTERSECT",VERTEX,{"derivedFrom":[makeQuery(id+"F19.boolean.opBoolean","INTERSECT",EDGE,{"derivedFrom":[makeQuery(id+"F2.opChamfer","BLEND_FACE",FACE,{"disambiguationData":[OSD([subQ4])]}),subQ3]}),subQ2,subQ1]}),1.0]])],"derivedFrom":subQ1}),makeQuery(id+"F20.imprint","IMPRINT",EDGE,{"derivedFrom":subQ0})]});}
            var Q3;
            Q3=makeQuery(id+"F21.opExtrude","CAP_EDGE",EDGE,{"disambiguationData":[OSD([sQuery(id+"F20.wireOp",EDGE,"E52"),sQuery(id+"F20.wireOp",EDGE,"E55"),sQuery(id+"F20.wireOp",EDGE,"E57")])],"isStart":true});
            var Q4;
            Q4=makeQuery(id+"F21.opExtrude","SWEPT_EDGE",EDGE,{"disambiguationData":[OSD([sQuery(id+"F20.wireOp",EDGE,"E56"),sQuery(id+"F20.wireOp",EDGE,"E57")])]});
            var Q5;
            Q5=makeQuery(id+"F23.opExtrude","CAP_EDGE",EDGE,{"disambiguationData":[OSD([sQuery(id+"F22.wireOp",EDGE,"E77.MirrorCS")])],"isStart":true});
            var Q6;
            {var subQ0=sQuery(id+"F22.wireOp",EDGE,"E77.MirrorCS");var subQ1=sQuery(id+"F18.wireOp",EDGE,"E44.MirrorCS");var subQ2=makeQuery(id+"F19.opExtrude","SWEPT_FACE",FACE,{"disambiguationData":[OSD([subQ1])]});var subQ3=sQuery(id+"F0.wireOp",EDGE,"E0.left");var subQ4=makeQuery(id+"F22.imprint","INTERSECT",VERTEX,{"derivedFrom":[makeQuery(id+"F19.boolean.opBoolean","INTERSECT",EDGE,{"derivedFrom":[makeQuery(id+"F5.opShell","OFFSET_FACE",FACE,{"disambiguationData":[OSD([subQ3])]}),subQ2]}),subQ0]});Q6=makeQuery(id+"F23.opExtrude","TWEAK_EDGE",EDGE,{"derivedFrom":[makeQuery(id+"F19.boolean.opBoolean","COPY",FACE,{"derivedFrom":makeQuery(id+"F19.opExtrude","SWEPT_FACE",FACE,{"disambiguationData":[OSD([sQuery(id+"F18.wireOp",EDGE,"E40.bottom")])]})}),makeQuery(id+"F22.imprint","IMPRINT",EDGE,{"disambiguationData":[TD([[subQ4,1.0]])],"derivedFrom":subQ0}),makeQuery(id+"F22.imprint","IMPRINT",EDGE,{"disambiguationData":[TD([[makeQuery(id+"F22.imprint","INTERSECT",VERTEX,{"derivedFrom":[sQuery(id+"F22.wireOp",EDGE,"E76.MirrorCS"),subQ0]}),1.0]])],"derivedFrom":subQ0})]});}
            var Q7;
            Q7=makeQuery(id+"F23.opExtrude","SWEPT_EDGE",EDGE,{"disambiguationData":[OSD([sQuery(id+"F22.wireOp",EDGE,"E76.MirrorCS"),sQuery(id+"F22.wireOp",EDGE,"E77.MirrorCS")])]});
            var Q8;
            Q8=makeQuery(id+"F23.opExtrude","CAP_EDGE",EDGE,{"disambiguationData":[OSD([sQuery(id+"F22.wireOp",EDGE,"E75.MirrorCS"),sQuery(id+"F22.wireOp",EDGE,"E76.MirrorCS")])],"isStart":true});
            var Q9;
            {var subQ0=sQuery(id+"F22.wireOp",EDGE,"E76.MirrorCS");var subQ1=sQuery(id+"F22.wireOp",EDGE,"E75.MirrorCS");var subQ2=makeQuery(id+"F19.opExtrude","SWEPT_FACE",FACE,{"disambiguationData":[OSD([sQuery(id+"F18.wireOp",EDGE,"E44.MirrorCS")])]});var subQ3=sQuery(id+"F0.wireOp",EDGE,"E0.left");var subQ4=makeQuery(id+"F22.imprint","INTERSECT",VERTEX,{"derivedFrom":[makeQuery(id+"F19.boolean.opBoolean","INTERSECT",EDGE,{"derivedFrom":[makeQuery(id+"F5.opShell","OFFSET_FACE",FACE,{"disambiguationData":[OSD([subQ3])]}),subQ2]}),subQ0]});Q9=makeQuery(id+"F23.opExtrude","TWEAK_EDGE",EDGE,{"derivedFrom":[makeQuery(id+"F19.boolean.opBoolean","COPY",FACE,{"derivedFrom":makeQuery(id+"F19.opExtrude","SWEPT_FACE",FACE,{"disambiguationData":[OSD([sQuery(id+"F18.wireOp",EDGE,"E40.bottom")])]})}),makeQuery(id+"F22.imprint","IMPRINT",EDGE,{"derivedFrom":subQ1}),makeQuery(id+"F22.imprint","IMPRINT",EDGE,{"disambiguationData":[TD([[makeQuery(id+"F22.imprint","INTERSECT",VERTEX,{"derivedFrom":[subQ0,sQuery(id+"F22.wireOp",EDGE,"E77.MirrorCS")]}),-1.0]])],"derivedFrom":subQ0}),makeQuery(id+"F22.imprint","IMPRINT",EDGE,{"disambiguationData":[TD([[subQ4,-1.0]])],"derivedFrom":subQ0})]});}
            var Q10;
            Q10=makeQuery(id+"F21.opExtrude","CAP_EDGE",EDGE,{"disambiguationData":[OSD([sQuery(id+"F20.wireOp",EDGE,"E63.MirrorCS")])],"isStart":true});
            var Q11;
            Q11=makeQuery(id+"F21.opExtrude","TWEAK_EDGE",EDGE,{"derivedFrom":[makeQuery(id+"F19.boolean.opBoolean","COPY",FACE,{"derivedFrom":makeQuery(id+"F19.opExtrude","SWEPT_FACE",FACE,{"disambiguationData":[OSD([sQuery(id+"F18.wireOp",EDGE,"E49.MirrorCS")])]})}),makeQuery(id+"F20.imprint","IMPRINT",EDGE,{"derivedFrom":sQuery(id+"F20.wireOp",EDGE,"E63.MirrorCS")})]});
            var Q12;
            Q12=makeQuery(id+"F21.opExtrude","SWEPT_EDGE",EDGE,{"disambiguationData":[OSD([sQuery(id+"F20.wireOp",EDGE,"E63.MirrorCS"),sQuery(id+"F20.wireOp",EDGE,"E64.MirrorCS")])]});
            var Q13;
            Q13=makeQuery(id+"F21.opExtrude","CAP_EDGE",EDGE,{"disambiguationData":[OSD([sQuery(id+"F20.wireOp",EDGE,"E64.MirrorCS"),sQuery(id+"F20.wireOp",EDGE,"E65.MirrorCS"),sQuery(id+"F20.wireOp",EDGE,"E66.MirrorCS")])],"isStart":true});
            var Q14;
            Q14=makeQuery(id+"F21.opExtrude","TWEAK_EDGE",EDGE,{"derivedFrom":[makeQuery(id+"F19.boolean.opBoolean","COPY",FACE,{"derivedFrom":makeQuery(id+"F19.opExtrude","SWEPT_FACE",FACE,{"disambiguationData":[OSD([sQuery(id+"F18.wireOp",EDGE,"E49.MirrorCS")])]})}),makeQuery(id+"F20.imprint","IMPRINT",EDGE,{"derivedFrom":sQuery(id+"F20.wireOp",EDGE,"E64.MirrorCS")}),makeQuery(id+"F20.imprint","IMPRINT",EDGE,{"derivedFrom":sQuery(id+"F20.wireOp",EDGE,"E65.MirrorCS")}),makeQuery(id+"F20.imprint","IMPRINT",EDGE,{"derivedFrom":sQuery(id+"F20.wireOp",EDGE,"E66.MirrorCS")})]});
            var Q15;
            Q15=makeQuery(id+"F23.opExtrude","TWEAK_EDGE",EDGE,{"derivedFrom":[makeQuery(id+"F19.boolean.opBoolean","COPY",FACE,{"derivedFrom":makeQuery(id+"F19.opExtrude","SWEPT_FACE",FACE,{"disambiguationData":[OSD([sQuery(id+"F18.wireOp",EDGE,"E40.bottom")])]})}),makeQuery(id+"F22.imprint","IMPRINT",EDGE,{"derivedFrom":sQuery(id+"F22.wireOp",EDGE,"E73.MirrorCS")})]});
            var Q16;
            Q16=makeQuery(id+"F23.opExtrude","CAP_EDGE",EDGE,{"disambiguationData":[OSD([sQuery(id+"F22.wireOp",EDGE,"E73.MirrorCS")])],"isStart":true});
            var Q17;
            Q17=makeQuery(id+"F23.opExtrude","SWEPT_EDGE",EDGE,{"disambiguationData":[OSD([sQuery(id+"F22.wireOp",EDGE,"E72.MirrorCS"),sQuery(id+"F22.wireOp",EDGE,"E73.MirrorCS")])]});
            var Q18;
            Q18=makeQuery(id+"F23.opExtrude","CAP_EDGE",EDGE,{"disambiguationData":[OSD([sQuery(id+"F22.wireOp",EDGE,"E69.MirrorCS"),sQuery(id+"F22.wireOp",EDGE,"E72.MirrorCS")])],"isStart":true});
            var Q19;
            Q19=makeQuery(id+"F23.opExtrude","TWEAK_EDGE",EDGE,{"derivedFrom":[makeQuery(id+"F19.boolean.opBoolean","COPY",FACE,{"derivedFrom":makeQuery(id+"F19.opExtrude","SWEPT_FACE",FACE,{"disambiguationData":[OSD([sQuery(id+"F18.wireOp",EDGE,"E40.bottom")])]})}),makeQuery(id+"F22.imprint","IMPRINT",EDGE,{"derivedFrom":sQuery(id+"F22.wireOp",EDGE,"E69.MirrorCS")}),makeQuery(id+"F22.imprint","IMPRINT",EDGE,{"derivedFrom":sQuery(id+"F22.wireOp",EDGE,"E72.MirrorCS")})]});
            fillet(context, id + "F24", {"entities" : qUnion([Q0, Q1, Q2, Q3, Q4, Q5, Q6, Q7, Q8, Q9, Q10, Q11, Q12, Q13, Q14, Q15, Q16, Q17, Q18, Q19]), "radius" : .5 * mm, "tangentPropagation" : true, "allowEdgeOverflow" : false});
        }
        {
            var Q0;
            Q0=makeQuery(id+"F8.opExtrude","CAP_FACE",FACE,{"disambiguationData":[OSD([sQuery(id+"F7.wireOp",EDGE,"E1.bottom"),sQuery(id+"F7.wireOp",EDGE,"E1.top"),sQuery(id+"F7.wireOp",EDGE,"E1.left"),sQuery(id+"F7.wireOp",EDGE,"E1.right")])],"isStart":true});
            var sketch = newSketch(context, id + "F25", { "sketchPlane" : qUnion([Q0])});
            skLineSegment(sketch, "E79.0", {"start": v(0, 6) * mm, "end": v(0, 114) * mm, "construction": true});
            skLineSegment(sketch, "E80.0", {"start": v(6, 120) * mm, "end": v(74, 120) * mm, "construction": true});
            skLineSegment(sketch, "E81.0", {"start": v(80, 114) * mm, "end": v(80, 6) * mm, "construction": true});
            skLineSegment(sketch, "E82.0", {"start": v(74, 0) * mm, "end": v(6, 0) * mm, "construction": true});
            skLineSegment(sketch, "E83.bottom", {"start": v(0, 0) * mm, "end": v(80, 0) * mm});
            skLineSegment(sketch, "E83.top", {"start": v(0, 120) * mm, "end": v(80, 120) * mm});
            skLineSegment(sketch, "E83.left", {"start": v(0, 0) * mm, "end": v(0, 120) * mm});
            skLineSegment(sketch, "E83.right", {"start": v(80, 0) * mm, "end": v(80, 120) * mm});
            skLineSegment(sketch, "E84.bottom", {"start": v(13.65, 103) * mm, "end": v(66.35, 103) * mm, "construction": true});
            skLineSegment(sketch, "E84.top", {"start": v(13.65, 106.25) * mm, "end": v(66.35, 106.25) * mm, "construction": true});
            skLineSegment(sketch, "E84.left", {"start": v(13.65, 103) * mm, "end": v(13.65, 106.25) * mm, "construction": true});
            skLineSegment(sketch, "E84.right", {"start": v(66.35, 103) * mm, "end": v(66.35, 106.25) * mm, "construction": true});
            skLineSegment(sketch, "E85.bottom", {"start": v(13.65, 17) * mm, "end": v(66.35, 17) * mm, "construction": true});
            skLineSegment(sketch, "E85.top", {"start": v(13.65, 13.75) * mm, "end": v(66.35, 13.75) * mm, "construction": true});
            skLineSegment(sketch, "E85.left", {"start": v(13.65, 17) * mm, "end": v(13.65, 13.75) * mm, "construction": true});
            skLineSegment(sketch, "E85.right", {"start": v(66.35, 17) * mm, "end": v(66.35, 13.75) * mm, "construction": true});
            skCircle(sketch, "E86", {"center": v(40, 60) * mm, "radius": 18.62 * mm, "construction": true});
            skLineSegment(sketch, "E87.bottom", {"start": v(12, 12) * mm, "end": v(68, 12) * mm, "construction": true});
            skLineSegment(sketch, "E87.top", {"start": v(12, 108) * mm, "end": v(68, 108) * mm, "construction": true});
            skLineSegment(sketch, "E87.left", {"start": v(12, 12) * mm, "end": v(12, 108) * mm, "construction": true});
            skLineSegment(sketch, "E87.right", {"start": v(68, 12) * mm, "end": v(68, 108) * mm, "construction": true});
            skSolve(sketch);
        }
        {
            var Q0;
            Q0 = qSketchRegion(id + "F25", true);
            extrude(context, id + "F26", {"entities" : qUnion([Q0]), "depth" : 10 * mm});
        }
        {
            var Q0;
            Q0=makeQuery(id+"F26.opExtrude","SWEPT_EDGE",EDGE,{"disambiguationData":[OSD([sQuery(id+"F25.wireOp",EDGE,"E83.top"),sQuery(id+"F25.wireOp",EDGE,"E83.left")])]});
            var Q1;
            Q1=makeQuery(id+"F26.opExtrude","CAP_EDGE",EDGE,{"disambiguationData":[OSD([sQuery(id+"F25.wireOp",EDGE,"E83.left")])],"isStart":true});
            var Q2;
            Q2=makeQuery(id+"F26.opExtrude","CAP_EDGE",EDGE,{"disambiguationData":[OSD([sQuery(id+"F25.wireOp",EDGE,"E83.top")])],"isStart":true});
            var Q3;
            Q3=makeQuery(id+"F26.opExtrude","SWEPT_EDGE",EDGE,{"disambiguationData":[OSD([sQuery(id+"F25.wireOp",EDGE,"E83.top"),sQuery(id+"F25.wireOp",EDGE,"E83.right")])]});
            var Q4;
            Q4=makeQuery(id+"F26.opExtrude","CAP_EDGE",EDGE,{"disambiguationData":[OSD([sQuery(id+"F25.wireOp",EDGE,"E83.right")])],"isStart":true});
            var Q5;
            Q5=makeQuery(id+"F26.opExtrude","SWEPT_EDGE",EDGE,{"disambiguationData":[OSD([sQuery(id+"F25.wireOp",EDGE,"E83.bottom"),sQuery(id+"F25.wireOp",EDGE,"E83.right")])]});
            var Q6;
            Q6=makeQuery(id+"F26.opExtrude","CAP_EDGE",EDGE,{"disambiguationData":[OSD([sQuery(id+"F25.wireOp",EDGE,"E83.bottom")])],"isStart":true});
            var Q7;
            Q7=makeQuery(id+"F26.opExtrude","SWEPT_EDGE",EDGE,{"disambiguationData":[OSD([sQuery(id+"F25.wireOp",EDGE,"E83.bottom"),sQuery(id+"F25.wireOp",EDGE,"E83.left")])]});
            fillet(context, id + "F27", {"entities" : qUnion([Q0, Q1, Q2, Q3, Q4, Q5, Q6, Q7]), "radius" : 6 * mm, "tangentPropagation" : true, "allowEdgeOverflow" : false});
        }
        {
            var Q0;
            Q0=makeQuery(id+"F26.opExtrude","CAP_FACE",FACE,{"disambiguationData":[OSD([sQuery(id+"F25.wireOp",EDGE,"E83.bottom"),sQuery(id+"F25.wireOp",EDGE,"E83.top"),sQuery(id+"F25.wireOp",EDGE,"E83.left"),sQuery(id+"F25.wireOp",EDGE,"E83.right")])],"isStart":false});
            shell(context, id + "F28", {"entities" : qUnion([Q0]), "thickness" : 1.8 * mm});
        }
        {
            var Q0;
            Q0=makeQuery(id+"F8.opExtrude","CAP_FACE",FACE,{"disambiguationData":[OSD([sQuery(id+"F7.wireOp",EDGE,"E1.bottom"),sQuery(id+"F7.wireOp",EDGE,"E1.top"),sQuery(id+"F7.wireOp",EDGE,"E1.left"),sQuery(id+"F7.wireOp",EDGE,"E1.right")])],"isStart":true});
            var sketch = newSketch(context, id + "F29", { "sketchPlane" : qUnion([Q0])});
            skCircle(sketch, "E88", {"center": v(40, 60) * mm, "radius": 18.62 * mm});
            skPoint(sketch, "E88.first.point", {"position": v(33.23, 77.35) * mm});
            skPoint(sketch, "E88.second.point", {"position": v(58.47, 62.38) * mm});
            skPoint(sketch, "E88.third.point", {"position": v(31.23, 43.57) * mm});
            skLineSegment(sketch, "E89.bottom", {"start": v(13.65, 106.25) * mm, "end": v(66.35, 106.25) * mm});
            skLineSegment(sketch, "E89.top", {"start": v(13.65, 103) * mm, "end": v(66.35, 103) * mm});
            skLineSegment(sketch, "E89.left", {"start": v(13.65, 106.25) * mm, "end": v(13.65, 103) * mm});
            skLineSegment(sketch, "E89.right", {"start": v(66.35, 106.25) * mm, "end": v(66.35, 103) * mm});
            skLineSegment(sketch, "E90.bottom", {"start": v(13.65, 17) * mm, "end": v(66.35, 17) * mm});
            skLineSegment(sketch, "E90.top", {"start": v(13.65, 13.75) * mm, "end": v(66.35, 13.75) * mm});
            skLineSegment(sketch, "E90.left", {"start": v(13.65, 17) * mm, "end": v(13.65, 13.75) * mm});
            skLineSegment(sketch, "E90.right", {"start": v(66.35, 17) * mm, "end": v(66.35, 13.75) * mm});
            skSolve(sketch);
        }
        {
            var Q0;
            Q0 = qSketchRegion(id + "F29", true);
            var Q1;
            Q1=makeQuery(id+"F28.opShell","OFFSET_FACE",FACE,{"disambiguationData":[OSD([sQuery(id+"F25.wireOp",EDGE,"E83.bottom"),sQuery(id+"F25.wireOp",EDGE,"E83.top"),sQuery(id+"F25.wireOp",EDGE,"E83.left"),sQuery(id+"F25.wireOp",EDGE,"E83.right")])]});
            extrude(context, id + "F30", {"entities" : qUnion([Q0]), "operationType" : NewBodyOperationType.REMOVE, "endBound" : BoundingType.UP_TO_SURFACE, "endBoundEntityFace" : qUnion([Q1]), "depth" : 25 * mm});
        }
        {
            var Q0;
            Q0=makeQuery(id+"F26.opExtrude","CAP_FACE",FACE,{"disambiguationData":[OSD([sQuery(id+"F25.wireOp",EDGE,"E83.bottom"),sQuery(id+"F25.wireOp",EDGE,"E83.top"),sQuery(id+"F25.wireOp",EDGE,"E83.left"),sQuery(id+"F25.wireOp",EDGE,"E83.right")])],"isStart":false});
            var sketch = newSketch(context, id + "F31", { "sketchPlane" : qUnion([Q0])});
            skLineSegment(sketch, "E91.bottom", {"start": v(6, 1.8) * mm, "end": v(74, 1.8) * mm});
            skLineSegment(sketch, "E91.top", {"start": v(6, 118.2) * mm, "end": v(74, 118.2) * mm});
            skLineSegment(sketch, "E91.left", {"start": v(1.8, 6) * mm, "end": v(1.8, 114) * mm});
            skLineSegment(sketch, "E91.right", {"start": v(78.2, 6) * mm, "end": v(78.2, 114) * mm});
            skPoint(sketch, "E92.visualSharp", {"position": v(1.8, 118.2) * mm});
            skArc(sketch, "E92.filletArc", {"start": v(6, 118.2) * mm, "mid": v(3.03, 116.97) * mm, "end": v(1.8, 114) * mm});
            skPoint(sketch, "E93.visualSharp", {"position": v(78.2, 118.2) * mm});
            skArc(sketch, "E93.filletArc", {"start": v(78.2, 114) * mm, "mid": v(76.97, 116.97) * mm, "end": v(74, 118.2) * mm});
            skPoint(sketch, "E94.visualSharp", {"position": v(1.8, 1.8) * mm});
            skArc(sketch, "E94.filletArc", {"start": v(1.8, 6) * mm, "mid": v(3.03, 3.03) * mm, "end": v(6, 1.8) * mm});
            skPoint(sketch, "E95.visualSharp", {"position": v(78.2, 1.8) * mm});
            skArc(sketch, "E95.filletArc", {"start": v(74, 1.8) * mm, "mid": v(76.97, 3.03) * mm, "end": v(78.2, 6) * mm});
            skLineSegment(sketch, "E96.0", {"start": v(6, 117.2) * mm, "end": v(74, 117.2) * mm});
            skLineSegment(sketch, "E97.0", {"start": v(2.8, 6) * mm, "end": v(2.8, 114) * mm});
            skLineSegment(sketch, "E98.0", {"start": v(6, 2.8) * mm, "end": v(74, 2.8) * mm});
            skLineSegment(sketch, "E99.0", {"start": v(77.2, 6) * mm, "end": v(77.2, 114) * mm});
            skArc(sketch, "E100.0", {"start": v(6, 117.2) * mm, "mid": v(3.74, 116.26) * mm, "end": v(2.8, 114) * mm});
            skArc(sketch, "E101.0", {"start": v(77.2, 114) * mm, "mid": v(76.26, 116.26) * mm, "end": v(74, 117.2) * mm});
            skArc(sketch, "E102.0", {"start": v(74, 2.8) * mm, "mid": v(76.26, 3.74) * mm, "end": v(77.2, 6) * mm});
            skArc(sketch, "E103.0", {"start": v(2.8, 6) * mm, "mid": v(3.74, 3.74) * mm, "end": v(6, 2.8) * mm});
            skSolve(sketch);
        }
        {
            var Q0;
            Q0=makeQuery(id+"F31.imprint","IMPRINT",FACE,{"disambiguationData":[TD([[makeQuery(id+"F31.imprint","IMPRINT",EDGE,{"derivedFrom":sQuery(id+"F31.wireOp",EDGE,"E91.bottom")}),1.0]])]});
            extrude(context, id + "F32", {"entities" : qUnion([Q0]), "operationType" : NewBodyOperationType.ADD, "oppositeDirection" : true, "depth" : 1 * mm});
        }
        {
            var Q0;
            Q0=makeQuery(id+"F32.opExtrude","SWEPT_FACE",FACE,{"disambiguationData":[OSD([sQuery(id+"F31.wireOp",EDGE,"E97.0")])]});
            fillet(context, id + "F33", {"entities" : qUnion([Q0]), "radius" : .5 * mm, "tangentPropagation" : true, "allowEdgeOverflow" : false});
        }
        {
            var Q0;
            {var subQ0=sQuery(id+"F0.wireOp",EDGE,"E0.right");var subQ1=sQuery(id+"F0.wireOp",EDGE,"E0.left");var subQ2=sQuery(id+"F0.wireOp",EDGE,"E0.top");var subQ3=sQuery(id+"F0.wireOp",EDGE,"E0.bottom");Q0=makeQuery(id+"F5.opShell","OFFSET_FACE",FACE,{"disambiguationData":[OSD([subQ3,subQ2,subQ1,subQ0]),TDD([makeQuery(id+"F1.opExtrude","CAP_FACE",FACE,{"disambiguationData":[OSD([subQ3,subQ2,subQ1,subQ0])],"isStart":true})])]});}
            var sketch = newSketch(context, id + "F34", { "sketchPlane" : qUnion([Q0])});
            skCircle(sketch, "E104", {"center": v(40, -60) * mm, "radius": 18.5 * mm});
            skCircle(sketch, "E105.0", {"center": v(40, -60) * mm, "radius": 21.5 * mm});
            skLineSegment(sketch, "E106", {"start": v(40, -38.5) * mm, "end": v(40, -78.62) * mm, "construction": true});
            skLineSegment(sketch, "E107", {"start": v(39, -38.52) * mm, "end": v(39, -41.4) * mm, "construction": true});
            skLineSegment(sketch, "E108.MirrorCS", {"start": v(41, -38.52) * mm, "end": v(41, -41.4) * mm, "construction": true});
            skLineSegment(sketch, "E109", {"start": v(40, -60) * mm, "end": v(61.5, -60) * mm, "construction": true});
            skLineSegment(sketch, "E110.MirrorCS", {"start": v(41, -81.48) * mm, "end": v(41, -78.6) * mm, "construction": true});
            skLineSegment(sketch, "E111.MirrorCS", {"start": v(39, -81.48) * mm, "end": v(39, -78.6) * mm, "construction": true});
            skSolve(sketch);
        }
        {
            var Q0;
            Q0=makeQuery(id+"F34.imprint","IMPRINT",FACE,{"disambiguationData":[TD([[makeQuery(id+"F34.imprint","IMPRINT",EDGE,{"derivedFrom":sQuery(id+"F34.wireOp",EDGE,"E105.0")}),1.0]])]});
            extrude(context, id + "F35", {"entities" : qUnion([Q0]), "operationType" : NewBodyOperationType.ADD, "depth" : 25 * mm});
        }
        {
            var Q0;
            Q0=makeQuery(id+"F35.opExtrude","SWEPT_FACE",FACE,{"disambiguationData":[OSD([sQuery(id+"F0.wireOp",EDGE,"E0.bottom"),sQuery(id+"F0.wireOp",EDGE,"E0.top"),sQuery(id+"F0.wireOp",EDGE,"E0.left"),sQuery(id+"F0.wireOp",EDGE,"E0.right"),sQuery(id+"F9.wireOp",EDGE,"E20")])]});
            cPlane(context, id + "F36", {"entities" : qUnion([Q0]), "cplaneType" : CPlaneType.LINE_ANGLE, "offset" : 25 * mm, "angle" : 90 * degree, "width" : 150 * mm, "height" : 150 * mm});
        }
        {
            var Q0;
            Q0=qCreatedBy(id+"F36.planeOp",FACE);
            var sketch = newSketch(context, id + "F37", { "sketchPlane" : qUnion([Q0])});
            skLineSegment(sketch, "E112", {"start": v(-18.5, -1.8) * mm, "end": v(-18.5, -26.8) * mm, "construction": true});
            skLineSegment(sketch, "E113", {"start": v(-61.5, -26.8) * mm, "end": v(-61.5, -1.8) * mm, "construction": true});
            skLineSegment(sketch, "E114.0", {"start": v(-18.5, -26.8) * mm, "end": v(-61.5, -26.8) * mm, "construction": true});
            skLineSegment(sketch, "E115.0", {"start": v(-18.5, -1.8) * mm, "end": v(-61.5, -1.8) * mm, "construction": true});
            skLineSegment(sketch, "E116", {"start": v(-40, -26.8) * mm, "end": v(-40, -1.8) * mm, "construction": true});
            skLineSegment(sketch, "E117", {"start": v(-41, -6.8) * mm, "end": v(-41, -26.8) * mm});
            skLineSegment(sketch, "E118.MirrorCS", {"start": v(-39, -6.8) * mm, "end": v(-39, -26.8) * mm});
            skArc(sketch, "E119", {"start": v(-39, -6.8) * mm, "mid": v(-40, -5.8) * mm, "end": v(-41, -6.8) * mm});
            skPoint(sketch, "E120.orphan", {"position": v(-39, -6.8) * mm});
            skPoint(sketch, "E121.orphan", {"position": v(-41, -1.8) * mm});
            skPoint(sketch, "E122.orphan", {"position": v(-39, -1.8) * mm});
            skLineSegment(sketch, "E123", {"start": v(-41, -26.8) * mm, "end": v(-39, -26.8) * mm});
            skSolve(sketch);
        }
        {
            var Q0;
            Q0 = qSketchRegion(id + "F37", true);
            extrude(context, id + "F38", {"entities" : qUnion([Q0]), "operationType" : NewBodyOperationType.REMOVE, "endBound" : BoundingType.SYMMETRIC, "oppositeDirection" : true, "depth" : 45 * mm});
        }
        {
            var Q0;
            {var subQ0=sQuery(id+"F34.wireOp",EDGE,"E105.0");var subQ1=sQuery(id+"F9.wireOp",EDGE,"E20");var subQ2=sQuery(id+"F0.wireOp",EDGE,"E0.right");var subQ3=sQuery(id+"F0.wireOp",EDGE,"E0.left");var subQ4=sQuery(id+"F0.wireOp",EDGE,"E0.top");var subQ5=sQuery(id+"F0.wireOp",EDGE,"E0.bottom");Q0=makeQuery(id+"F38.boolean.opBoolean","SPLIT",FACE,{"disambiguationData":[TD([makeQuery(id+"F38.opExtrude","SWEPT_FACE",FACE,{"disambiguationData":[OSD([sQuery(id+"F37.wireOp",EDGE,"E117")])]})])],"derivedFrom":makeQuery(id+"F35.opExtrude","CAP_FACE",FACE,{"disambiguationData":[OSD([subQ5,subQ4,subQ3,subQ2,subQ1,subQ0])],"isStart":false})});}
            var Q1;
            {var subQ0=sQuery(id+"F34.wireOp",EDGE,"E105.0");var subQ1=sQuery(id+"F9.wireOp",EDGE,"E20");var subQ2=sQuery(id+"F0.wireOp",EDGE,"E0.right");var subQ3=sQuery(id+"F0.wireOp",EDGE,"E0.left");var subQ4=sQuery(id+"F0.wireOp",EDGE,"E0.top");var subQ5=sQuery(id+"F0.wireOp",EDGE,"E0.bottom");Q1=makeQuery(id+"F38.boolean.opBoolean","SPLIT",FACE,{"disambiguationData":[TD([makeQuery(id+"F38.opExtrude","SWEPT_FACE",FACE,{"disambiguationData":[OSD([sQuery(id+"F37.wireOp",EDGE,"E118.MirrorCS")])]})])],"derivedFrom":makeQuery(id+"F35.opExtrude","CAP_FACE",FACE,{"disambiguationData":[OSD([subQ5,subQ4,subQ3,subQ2,subQ1,subQ0])],"isStart":false})});}
            var Q2;
            Q2=makeQuery(id+"F38.boolean.opBoolean","COPY",FACE,{"disambiguationData":[OD(0.0)],"derivedFrom":makeQuery(id+"F38.opExtrude","SWEPT_FACE",FACE,{"disambiguationData":[OSD([sQuery(id+"F37.wireOp",EDGE,"E118.MirrorCS")])]})});
            var Q3;
            Q3=makeQuery(id+"F38.boolean.opBoolean","COPY",FACE,{"disambiguationData":[OD(1.0)],"derivedFrom":makeQuery(id+"F38.opExtrude","SWEPT_FACE",FACE,{"disambiguationData":[OSD([sQuery(id+"F37.wireOp",EDGE,"E118.MirrorCS")])]})});
            fillet(context, id + "F39", {"entities" : qUnion([Q0, Q1, Q2, Q3]), "radius" : 1 * mm, "tangentPropagation" : true, "allowEdgeOverflow" : false});
        }
        {
            var Q0;
            Q0=makeQuery(id+"F10.boolean.opBoolean","COPY",FACE,{"derivedFrom":makeQuery(id+"F10.opExtrude","SWEPT_FACE",FACE,{"disambiguationData":[OSD([sQuery(id+"F9.wireOp",EDGE,"E14.left")])]})});
            var sketch = newSketch(context, id + "F40", { "sketchPlane" : qUnion([Q0])});
            skLineSegment(sketch, "E124.0", {"start": v(13.75, 2.8) * mm, "end": v(17, 2.8) * mm, "construction": true});
            skLineSegment(sketch, "E125", {"start": v(13.75, -1.88) * mm, "end": v(13.75, 2.8) * mm});
            skLineSegment(sketch, "E126", {"start": v(17, -1.88) * mm, "end": v(17, 2.8) * mm});
            skLineSegment(sketch, "E127", {"start": v(17, 2.8) * mm, "end": v(19, 2.8) * mm});
            skLineSegment(sketch, "E128", {"start": v(19, 2.8) * mm, "end": v(19, 4.8) * mm});
            skLineSegment(sketch, "E129", {"start": v(19, 4.8) * mm, "end": v(15.38, 4.8) * mm});
            skPoint(sketch, "E129.endSnap0", {"position": v(15.38, 2.8) * mm});
            skLineSegment(sketch, "E130", {"start": v(17, -1.88) * mm, "end": v(13.75, -1.88) * mm});
            skLineSegment(sketch, "E131", {"start": v(15.38, 2.8) * mm, "end": v(15.38, -1.88) * mm, "construction": true});
            skLineSegment(sketch, "E132.MirrorCS", {"start": v(13.75, 2.8) * mm, "end": v(11.75, 2.8) * mm});
            skLineSegment(sketch, "E133.MirrorCS", {"start": v(11.75, 4.8) * mm, "end": v(15.38, 4.8) * mm});
            skLineSegment(sketch, "E134.MirrorCS", {"start": v(11.75, 2.8) * mm, "end": v(11.75, 4.8) * mm});
            skLineSegment(sketch, "E135", {"start": v(12, 4.55) * mm, "end": v(12, 3.05) * mm});
            skLineSegment(sketch, "E136", {"start": v(12, 3.05) * mm, "end": v(14, 3.05) * mm});
            skLineSegment(sketch, "E137", {"start": v(14, 3.05) * mm, "end": v(14, -1.63) * mm});
            skLineSegment(sketch, "E138", {"start": v(14, -1.63) * mm, "end": v(16.75, -1.63) * mm});
            skLineSegment(sketch, "E139", {"start": v(16.75, -1.63) * mm, "end": v(16.75, 3.05) * mm});
            skLineSegment(sketch, "E140", {"start": v(16.75, 3.05) * mm, "end": v(18.75, 3.05) * mm});
            skLineSegment(sketch, "E141", {"start": v(18.75, 3.05) * mm, "end": v(18.75, 4.55) * mm});
            skLineSegment(sketch, "E142", {"start": v(18.75, 4.55) * mm, "end": v(12, 4.55) * mm});
            skSolve(sketch);
        }
        {
            var Q0;
            Q0=makeQuery(id+"F40.imprint","IMPRINT",FACE,{"disambiguationData":[TD([[makeQuery(id+"F40.imprint","IMPRINT",EDGE,{"derivedFrom":sQuery(id+"F40.wireOp",EDGE,"E135")}),1.0]])]});
            var Q1;
            {var subQ0=sQuery(id+"F40.wireOp",EDGE,"E138");Q1=makeQuery(id+"F40.imprint","IMPRINT",FACE,{"disambiguationData":[TD([[makeQuery(id+"F40.imprint","IMPRINT",EDGE,{"derivedFrom":subQ0}),1.0]])]});}
            var Q2;
            Q2=makeQuery(id+"F30.boolean.opBoolean","COPY",FACE,{"derivedFrom":makeQuery(id+"F30.opExtrude","SWEPT_FACE",FACE,{"disambiguationData":[OSD([sQuery(id+"F29.wireOp",EDGE,"E90.right")])]})});
            extrude(context, id + "F41", {"entities" : qUnion([Q0, Q1]), "endBound" : BoundingType.UP_TO_SURFACE, "endBoundEntityFace" : qUnion([Q2]), "depth" : 25 * mm});
        }
        {
            var Q0;
            Q0=makeQuery(id+"F41.opExtrude","SWEPT_BODY",BODY,{"disambiguationData":[OSD([sQuery(id+"F40.wireOp",EDGE,"E135"),sQuery(id+"F40.wireOp",EDGE,"E136"),sQuery(id+"F40.wireOp",EDGE,"E137"),sQuery(id+"F40.wireOp",EDGE,"E138"),sQuery(id+"F40.wireOp",EDGE,"E139"),sQuery(id+"F40.wireOp",EDGE,"E140"),sQuery(id+"F40.wireOp",EDGE,"E141"),sQuery(id+"F40.wireOp",EDGE,"E142")])]});
            transform(context, id + "F42", {"entities" : qUnion([Q0]), "transformType" : TransformType.TRANSLATION_3D, "dx" : 0 * mm, "dy" : 89.25 * mm, "dz" : 0 * mm, "makeCopy" : true});
        }
        {
            var Q0;
            Q0=makeQuery(id+"F17.opBoolean","SPLIT",BODY,{"disambiguationData":[OD(1.0)],"derivedFrom":makeQuery(id+"F15.opExtrude","SWEPT_BODY",BODY,{"disambiguationData":[OSD([sQuery(id+"F14.wireOp",EDGE,"E26.0"),sQuery(id+"F14.wireOp",EDGE,"E26.1"),sQuery(id+"F14.wireOp",EDGE,"E26.2"),sQuery(id+"F14.wireOp",EDGE,"E26.3"),sQuery(id+"F14.wireOp",EDGE,"E31.bottom"),sQuery(id+"F14.wireOp",EDGE,"E31.top"),sQuery(id+"F14.wireOp",EDGE,"E31.left"),sQuery(id+"F14.wireOp",EDGE,"E31.right")])]})});
            deleteBodies(context, id + "F43", {"entities" : qUnion([Q0])});
        }
    });
